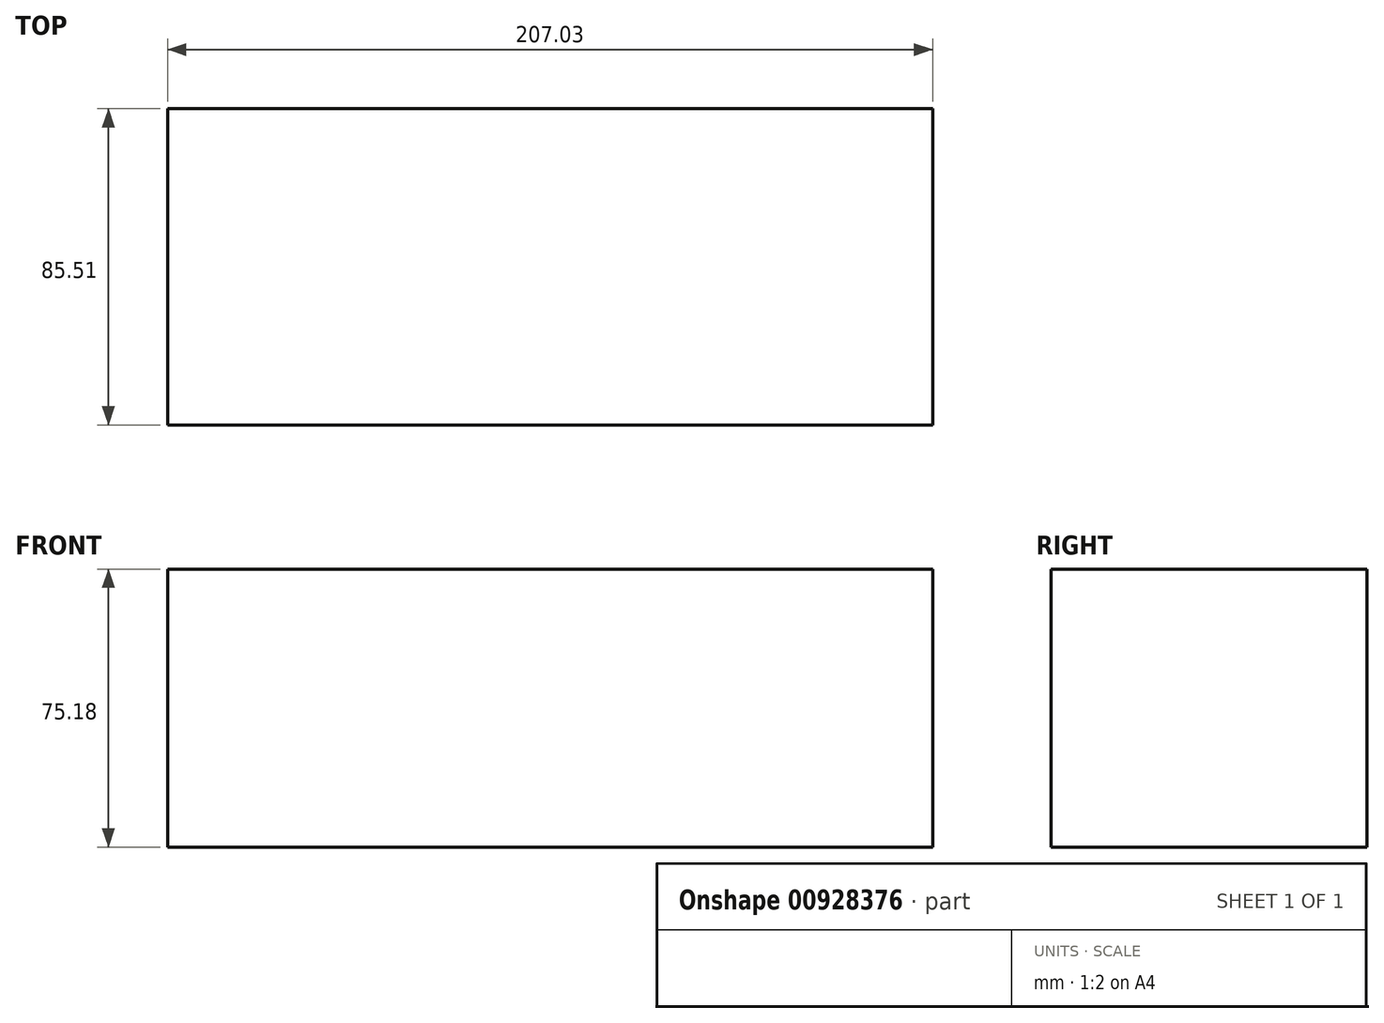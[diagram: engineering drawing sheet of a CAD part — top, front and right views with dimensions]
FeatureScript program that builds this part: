
annotation { "Feature Type Name" : "Feature", "Feature Type Description" : "" }
export const myFeature = defineFeature(function(context is Context, id is Id, definition is map)
    precondition{}
    {
        {
            var Q0;
            Q0=qCreatedBy(makeId("Top.planeOp"),FACE);
            var sketch = newSketch(context, id + "F0", { "sketchPlane" : qUnion([Q0])});
            skLineSegment(sketch, "E0.bottom", {"start": v(-108.52, -46.49) * mm, "end": v(98.5, -46.49) * mm});
            skLineSegment(sketch, "E0.top", {"start": v(-108.52, 39.02) * mm, "end": v(98.5, 39.02) * mm});
            skLineSegment(sketch, "E0.left", {"start": v(-108.52, -46.49) * mm, "end": v(-108.52, 39.02) * mm});
            skLineSegment(sketch, "E0.right", {"start": v(98.5, -46.49) * mm, "end": v(98.5, 39.02) * mm});
            skSolve(sketch);
        }
        {
            var Q0;
            Q0=makeQuery(id+"F0.imprint","IMPRINT",FACE,{"disambiguationData":[TD([[makeQuery(id+"F0.imprint","IMPRINT",EDGE,{"derivedFrom":sQuery(id+"F0.wireOp",EDGE,"E0.bottom")}),1.0]])]});
            extrude(context, id + "F1", {"entities" : qUnion([Q0]), "depth" : 75.18 * mm, "offsetDistance" : 25.4 * mm});
        }
    });
